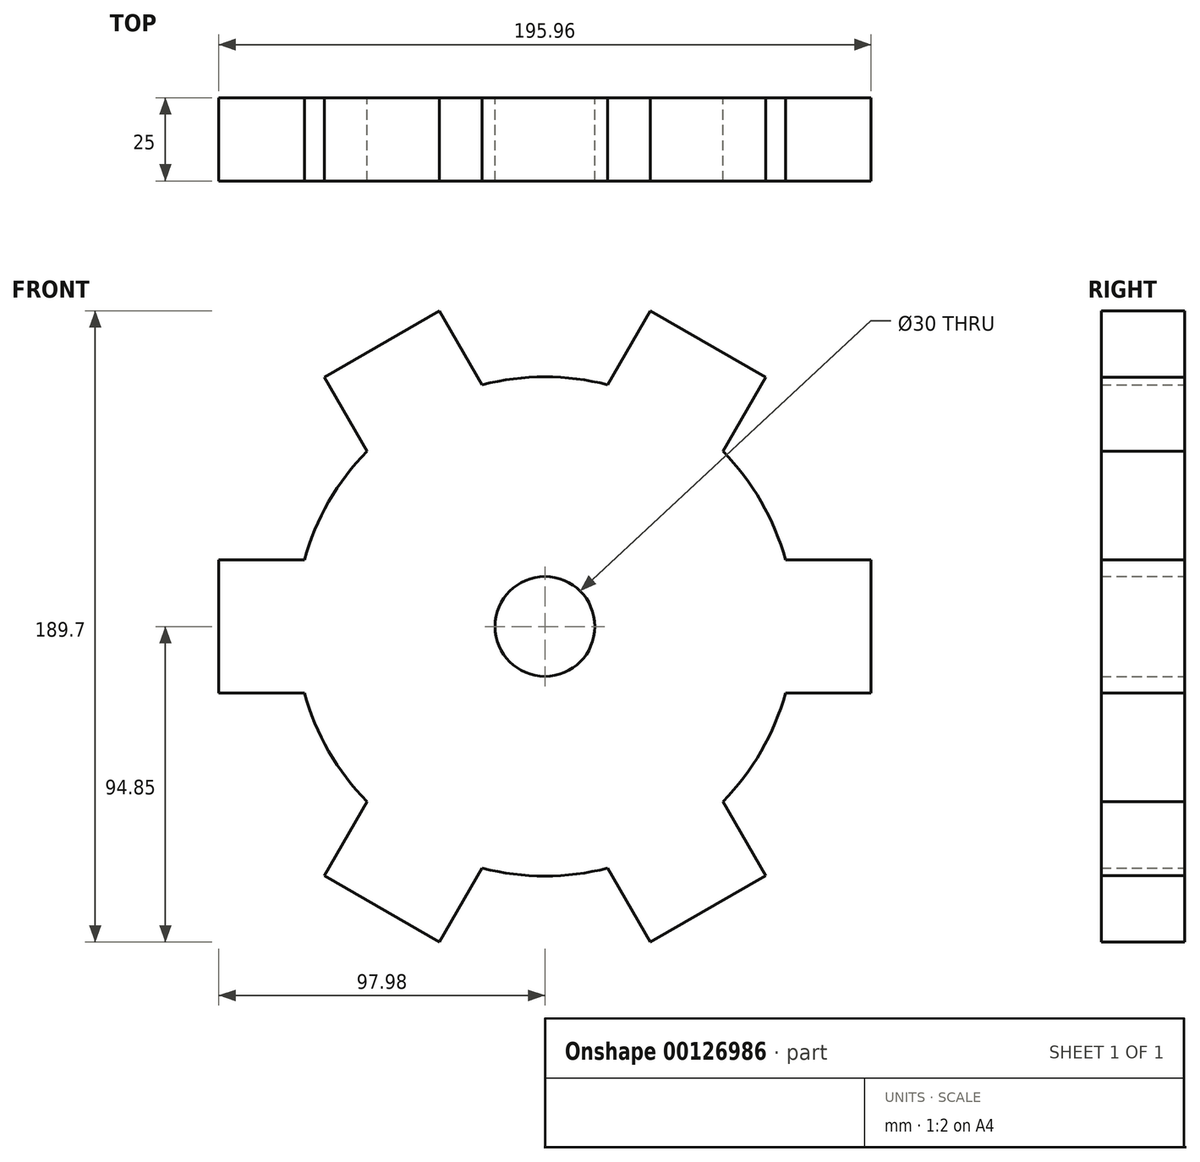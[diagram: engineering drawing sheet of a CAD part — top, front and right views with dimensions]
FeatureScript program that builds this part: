
annotation { "Feature Type Name" : "Feature", "Feature Type Description" : "" }
export const myFeature = defineFeature(function(context is Context, id is Id, definition is map)
    precondition{}
    {
        {
            var Q0;
            Q0=qCreatedBy(makeId("Front.planeOp"),FACE);
            var sketch = newSketch(context, id + "F0", { "sketchPlane" : qUnion([Q0])});
            skCircle(sketch, "E0", {"center": v(0, 0) * mm, "radius": 75 * mm});
            skLineSegment(sketch, "E1.right", {"start": v(-97.98, 20) * mm, "end": v(-97.98, -20) * mm});
            skLineSegment(sketch, "E2", {"start": v(-97.98, -20) * mm, "end": v(-72.28, -20) * mm});
            skLineSegment(sketch, "E3", {"start": v(-97.98, 20) * mm, "end": v(-72.28, 20) * mm});
            skArc(sketch, "E4", {"start": v(-72.28, -20) * mm, "mid": v(-75, 0) * mm, "end": v(-72.28, 20) * mm});
            skLineSegment(sketch, "E5.trimOffspring", {"start": v(-72.28, 20) * mm, "end": v(-97.98, 20) * mm});
            skLineSegment(sketch, "E6.trimOffspring", {"start": v(-72.28, -20) * mm, "end": v(-97.98, -20) * mm});
            skPoint(sketch, "E1.left.end.orphan", {"position": v(97.98, -20) * mm});
            skPoint(sketch, "E1.bottom.start.orphan", {"position": v(97.98, 20) * mm});
            skLineSegment(sketch, "E7.1.0", {"start": v(-53.46, -52.6) * mm, "end": v(-66.31, -74.85) * mm});
            skLineSegment(sketch, "E7.1.1", {"start": v(-66.31, -74.85) * mm, "end": v(-31.67, -94.85) * mm});
            skLineSegment(sketch, "E7.1.2", {"start": v(-18.82, -72.6) * mm, "end": v(-31.67, -94.85) * mm});
            skLineSegment(sketch, "E7.2.0", {"start": v(18.82, -72.6) * mm, "end": v(31.67, -94.85) * mm});
            skLineSegment(sketch, "E7.2.1", {"start": v(31.67, -94.85) * mm, "end": v(66.31, -74.85) * mm});
            skLineSegment(sketch, "E7.2.2", {"start": v(53.46, -52.6) * mm, "end": v(66.31, -74.85) * mm});
            skLineSegment(sketch, "E7.3.0", {"start": v(72.28, -20) * mm, "end": v(97.98, -20) * mm});
            skLineSegment(sketch, "E7.3.1", {"start": v(97.98, -20) * mm, "end": v(97.98, 20) * mm});
            skLineSegment(sketch, "E7.3.2", {"start": v(72.28, 20) * mm, "end": v(97.98, 20) * mm});
            skLineSegment(sketch, "E7.4.0", {"start": v(53.46, 52.6) * mm, "end": v(66.31, 74.85) * mm});
            skLineSegment(sketch, "E7.4.1", {"start": v(66.31, 74.85) * mm, "end": v(31.67, 94.85) * mm});
            skLineSegment(sketch, "E7.4.2", {"start": v(18.82, 72.6) * mm, "end": v(31.67, 94.85) * mm});
            skLineSegment(sketch, "E7.5.0", {"start": v(-18.82, 72.6) * mm, "end": v(-31.67, 94.85) * mm});
            skLineSegment(sketch, "E7.5.1", {"start": v(-31.67, 94.85) * mm, "end": v(-66.31, 74.85) * mm});
            skLineSegment(sketch, "E7.5.2", {"start": v(-53.46, 52.6) * mm, "end": v(-66.31, 74.85) * mm});
            skCircle(sketch, "E8", {"center": v(0, 0) * mm, "radius": 15 * mm});
            skSolve(sketch);
        }
        {
            var Q0;
            Q0=makeQuery(id+"F0.imprint","IMPRINT",FACE,{"disambiguationData":[TD([[makeQuery(id+"F0.imprint","IMPRINT",EDGE,{"derivedFrom":sQuery(id+"F0.wireOp",EDGE,"E1.right")}),1.0]])]});
            var Q1;
            {var subQ0=sQuery(id+"F0.wireOp",EDGE,"E7.1.0");Q1=makeQuery(id+"F0.imprint","IMPRINT",FACE,{"disambiguationData":[TD([[makeQuery(id+"F0.imprint","IMPRINT",EDGE,{"derivedFrom":subQ0}),1.0]])]});}
            var Q2;
            {var subQ0=sQuery(id+"F0.wireOp",EDGE,"E7.2.0");Q2=makeQuery(id+"F0.imprint","IMPRINT",FACE,{"disambiguationData":[TD([[makeQuery(id+"F0.imprint","IMPRINT",EDGE,{"derivedFrom":subQ0}),1.0]])]});}
            var Q3;
            {var subQ0=sQuery(id+"F0.wireOp",EDGE,"E7.3.0");Q3=makeQuery(id+"F0.imprint","IMPRINT",FACE,{"disambiguationData":[TD([[makeQuery(id+"F0.imprint","IMPRINT",EDGE,{"derivedFrom":subQ0}),1.0]])]});}
            var Q4;
            {var subQ0=sQuery(id+"F0.wireOp",EDGE,"E7.4.0");Q4=makeQuery(id+"F0.imprint","IMPRINT",FACE,{"disambiguationData":[TD([[makeQuery(id+"F0.imprint","IMPRINT",EDGE,{"derivedFrom":subQ0}),1.0]])]});}
            var Q5;
            {var subQ0=sQuery(id+"F0.wireOp",EDGE,"E7.5.0");Q5=makeQuery(id+"F0.imprint","IMPRINT",FACE,{"disambiguationData":[TD([[makeQuery(id+"F0.imprint","IMPRINT",EDGE,{"derivedFrom":subQ0}),1.0]])]});}
            var Q6;
            Q6=makeQuery(id+"F0.imprint","IMPRINT",FACE,{"disambiguationData":[TD([[makeQuery(id+"F0.imprint","IMPRINT",EDGE,{"derivedFrom":sQuery(id+"F0.wireOp",EDGE,"E8")}),-1.0]])]});
            extrude(context, id + "F1", {"entities" : qUnion([Q0, Q1, Q2, Q3, Q4, Q5, Q6]), "depth" : 25 * mm});
        }
    });
